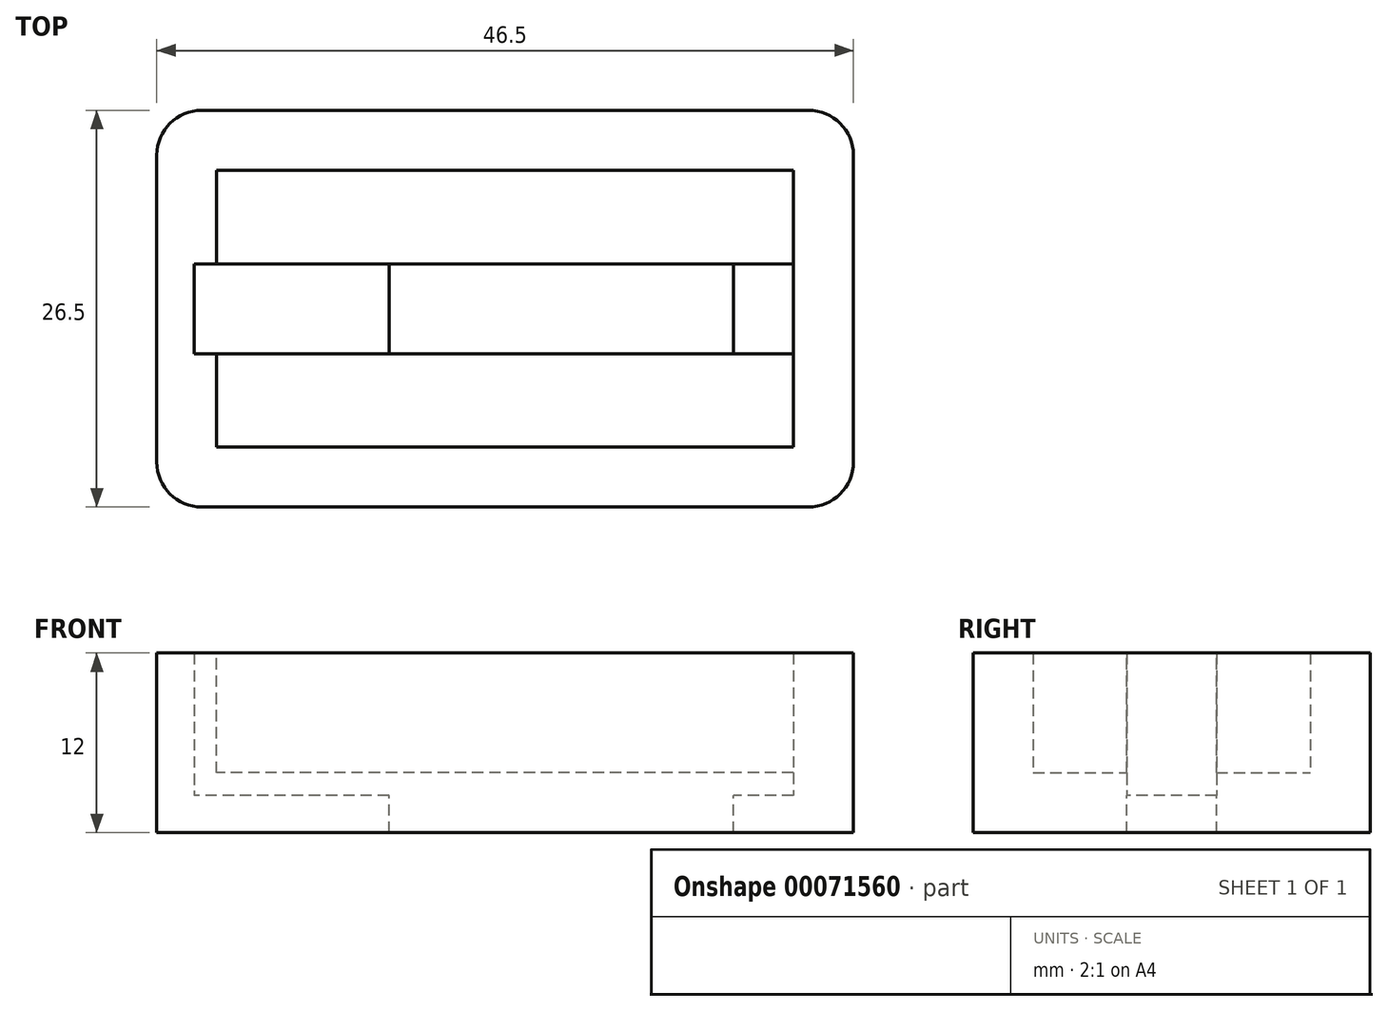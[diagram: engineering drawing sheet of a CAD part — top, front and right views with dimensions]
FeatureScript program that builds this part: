
annotation { "Feature Type Name" : "Feature", "Feature Type Description" : "" }
export const myFeature = defineFeature(function(context is Context, id is Id, definition is map)
    precondition{}
    {
        {
            var Q0;
            Q0=qCreatedBy(makeId("Top.planeOp"),FACE);
            var sketch = newSketch(context, id + "F0", { "sketchPlane" : qUnion([Q0])});
            skLineSegment(sketch, "E0.rect.bottom", {"start": v(19.25, -9.25) * mm, "end": v(-19.25, -9.25) * mm});
            skLineSegment(sketch, "E0.rect.top", {"start": v(19.25, 9.25) * mm, "end": v(-19.25, 9.25) * mm});
            skLineSegment(sketch, "E0.rect.left", {"start": v(19.25, -9.25) * mm, "end": v(19.25, 9.25) * mm});
            skLineSegment(sketch, "E0.rect.right", {"start": v(-19.25, -9.25) * mm, "end": v(-19.25, 9.25) * mm});
            skPoint(sketch, "E0.rect.middle", {"position": v(0, 0) * mm});
            skLineSegment(sketch, "E1.rect.bottom", {"start": v(23.25, 13.25) * mm, "end": v(-23.25, 13.25) * mm});
            skLineSegment(sketch, "E1.rect.top", {"start": v(23.25, -13.25) * mm, "end": v(-23.25, -13.25) * mm});
            skLineSegment(sketch, "E1.rect.left", {"start": v(23.25, 13.25) * mm, "end": v(23.25, -13.25) * mm});
            skLineSegment(sketch, "E1.rect.right", {"start": v(-23.25, 13.25) * mm, "end": v(-23.25, -13.25) * mm});
            skSolve(sketch);
        }
        {
            var Q0;
            Q0 = qSketchRegion(id + "F0", true);
            extrude(context, id + "F1", {"entities" : qUnion([Q0]), "depth" : 8 * mm});
        }
        {
            var Q0;
            Q0=makeQuery(id+"F1.opExtrude","CAP_FACE",FACE,{"disambiguationData":[OSD([sQuery(id+"F0.wireOp",EDGE,"E0.rect.bottom"),sQuery(id+"F0.wireOp",EDGE,"E0.rect.top"),sQuery(id+"F0.wireOp",EDGE,"E0.rect.left"),sQuery(id+"F0.wireOp",EDGE,"E0.rect.right"),sQuery(id+"F0.wireOp",EDGE,"E1.rect.bottom"),sQuery(id+"F0.wireOp",EDGE,"E1.rect.top"),sQuery(id+"F0.wireOp",EDGE,"E1.rect.left"),sQuery(id+"F0.wireOp",EDGE,"E1.rect.right")])],"isStart":true});
            var sketch = newSketch(context, id + "F2", { "sketchPlane" : qUnion([Q0])});
            skLineSegment(sketch, "E2.bottom", {"start": v(-23.25, 13.25) * mm, "end": v(23.25, 13.25) * mm});
            skLineSegment(sketch, "E2.top", {"start": v(-23.25, -13.25) * mm, "end": v(23.25, -13.25) * mm});
            skLineSegment(sketch, "E2.left", {"start": v(-23.25, 13.25) * mm, "end": v(-23.25, -13.25) * mm});
            skLineSegment(sketch, "E2.right", {"start": v(23.25, 13.25) * mm, "end": v(23.25, -13.25) * mm});
            skSolve(sketch);
        }
        {
            var Q0;
            Q0 = qSketchRegion(id + "F2", true);
            extrude(context, id + "F3", {"entities" : qUnion([Q0]), "operationType" : NewBodyOperationType.ADD, "depth" : 4 * mm});
        }
        {
            var Q0;
            Q0=qCreatedBy(makeId("Front.planeOp"),FACE);
            var sketch = newSketch(context, id + "F4", { "sketchPlane" : qUnion([Q0])});
            skLineSegment(sketch, "E3.bottom", {"start": v(19.25, 8) * mm, "end": v(-20.75, 8) * mm});
            skLineSegment(sketch, "E3.top", {"start": v(19.25, -1.5) * mm, "end": v(-20.75, -1.5) * mm});
            skLineSegment(sketch, "E3.left", {"start": v(19.25, 8) * mm, "end": v(19.25, -1.5) * mm});
            skLineSegment(sketch, "E3.right", {"start": v(-20.75, 8) * mm, "end": v(-20.75, -1.5) * mm});
            skPoint(sketch, "E4", {"position": v(-19.25, 8) * mm});
            skPoint(sketch, "E5", {"position": v(19.25, 0) * mm});
            skSolve(sketch);
        }
        {
            var Q0;
            Q0 = qSketchRegion(id + "F4", true);
            extrude(context, id + "F5", {"entities" : qUnion([Q0]), "operationType" : NewBodyOperationType.REMOVE, "endBound" : BoundingType.SYMMETRIC, "oppositeDirection" : true, "depth" : 6 * mm});
        }
        {
            var Q0;
            Q0=makeQuery(id+"F5.boolean.opBoolean","COPY",FACE,{"derivedFrom":makeQuery(id+"F5.opExtrude","SWEPT_FACE",FACE,{"disambiguationData":[OSD([sQuery(id+"F4.wireOp",EDGE,"E3.top")])]})});
            var sketch = newSketch(context, id + "F6", { "sketchPlane" : qUnion([Q0])});
            skLineSegment(sketch, "E6.bottom", {"start": v(-7.75, 3) * mm, "end": v(15.25, 3) * mm});
            skLineSegment(sketch, "E6.top", {"start": v(-7.75, -3) * mm, "end": v(15.25, -3) * mm});
            skLineSegment(sketch, "E6.left", {"start": v(-7.75, 3) * mm, "end": v(-7.75, -3) * mm});
            skLineSegment(sketch, "E6.right", {"start": v(15.25, 3) * mm, "end": v(15.25, -3) * mm});
            skSolve(sketch);
        }
        {
            var Q0;
            Q0=makeQuery(id+"F6.imprint","IMPRINT",FACE,{"disambiguationData":[TD([[makeQuery(id+"F6.imprint","IMPRINT",EDGE,{"derivedFrom":sQuery(id+"F6.wireOp",EDGE,"E6.bottom")}),1.0]])]});
            extrude(context, id + "F7", {"entities" : qUnion([Q0]), "operationType" : NewBodyOperationType.REMOVE, "endBound" : BoundingType.UP_TO_NEXT, "oppositeDirection" : true, "depth" : 25 * mm});
        }
        {
            var Q0;
            Q0=makeQuery(id+"F3.boolean.opBoolean","MERGE",EDGE,{"derivedFrom":[makeQuery(id+"F1.opExtrude","SWEPT_EDGE",EDGE,{"disambiguationData":[OSD([sQuery(id+"F0.wireOp",EDGE,"E1.rect.top"),sQuery(id+"F0.wireOp",EDGE,"E1.rect.right")])]}),makeQuery(id+"F3.opExtrude","SWEPT_EDGE",EDGE,{"disambiguationData":[OSD([sQuery(id+"F2.wireOp",EDGE,"E2.bottom"),sQuery(id+"F2.wireOp",EDGE,"E2.left")])]})]});
            var Q1;
            Q1=makeQuery(id+"F3.boolean.opBoolean","MERGE",EDGE,{"derivedFrom":[makeQuery(id+"F1.opExtrude","SWEPT_EDGE",EDGE,{"disambiguationData":[OSD([sQuery(id+"F0.wireOp",EDGE,"E1.rect.top"),sQuery(id+"F0.wireOp",EDGE,"E1.rect.left")])]}),makeQuery(id+"F3.opExtrude","SWEPT_EDGE",EDGE,{"disambiguationData":[OSD([sQuery(id+"F2.wireOp",EDGE,"E2.bottom"),sQuery(id+"F2.wireOp",EDGE,"E2.right")])]})]});
            var Q2;
            Q2=makeQuery(id+"F3.boolean.opBoolean","MERGE",EDGE,{"derivedFrom":[makeQuery(id+"F1.opExtrude","SWEPT_EDGE",EDGE,{"disambiguationData":[OSD([sQuery(id+"F0.wireOp",EDGE,"E1.rect.bottom"),sQuery(id+"F0.wireOp",EDGE,"E1.rect.right")])]}),makeQuery(id+"F3.opExtrude","SWEPT_EDGE",EDGE,{"disambiguationData":[OSD([sQuery(id+"F2.wireOp",EDGE,"E2.top"),sQuery(id+"F2.wireOp",EDGE,"E2.left")])]})]});
            var Q3;
            Q3=makeQuery(id+"F3.boolean.opBoolean","MERGE",EDGE,{"derivedFrom":[makeQuery(id+"F1.opExtrude","SWEPT_EDGE",EDGE,{"disambiguationData":[OSD([sQuery(id+"F0.wireOp",EDGE,"E1.rect.bottom"),sQuery(id+"F0.wireOp",EDGE,"E1.rect.left")])]}),makeQuery(id+"F3.opExtrude","SWEPT_EDGE",EDGE,{"disambiguationData":[OSD([sQuery(id+"F2.wireOp",EDGE,"E2.top"),sQuery(id+"F2.wireOp",EDGE,"E2.right")])]})]});
            fillet(context, id + "F8", {"entities" : qUnion([Q0, Q1, Q2, Q3]), "radius" : 3 * mm, "tangentPropagation" : true, "allowEdgeOverflow" : false});
        }
    });
